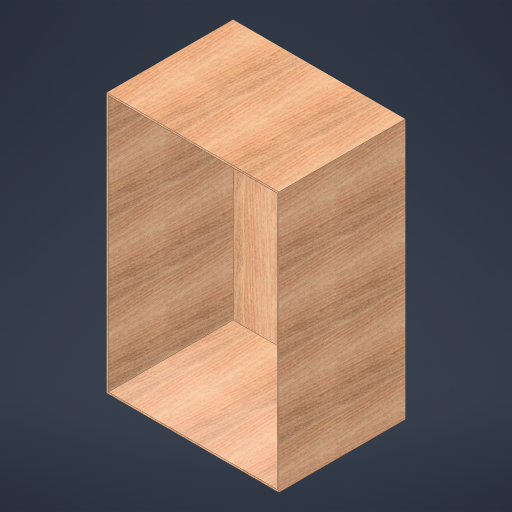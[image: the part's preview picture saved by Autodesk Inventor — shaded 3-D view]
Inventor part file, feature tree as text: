
AUTODESK INVENTOR PART (.ipt)
format: ipt  version: 2023.4 (Build 274418000, 418)  size: 445,440 bytes
history: native  units: in
note: dims shown in document units (in); Inventor stores cm internally (conversion verified against a paired STEP export)
features: extrude x2, sketch x1
ambient origin geometry x8: Origin, YZ Plane, XZ Plane, XY Plane, X Axis, Y Axis, Z Axis, Center Point
bodies: Solid1 (feature_tree)
feature tree (3):
  sketch  "Sketch1"  dims[d0=23.0in d1=35.0in d2=17.25in d3=0.0in d4=0.25in d5=17.0in d6=0.0in]
  extrude  "Extrusion1"  Depth=35.0in
  extrude  "Extrusion2"  Depth=17.25in TaperAngle=0.0deg
